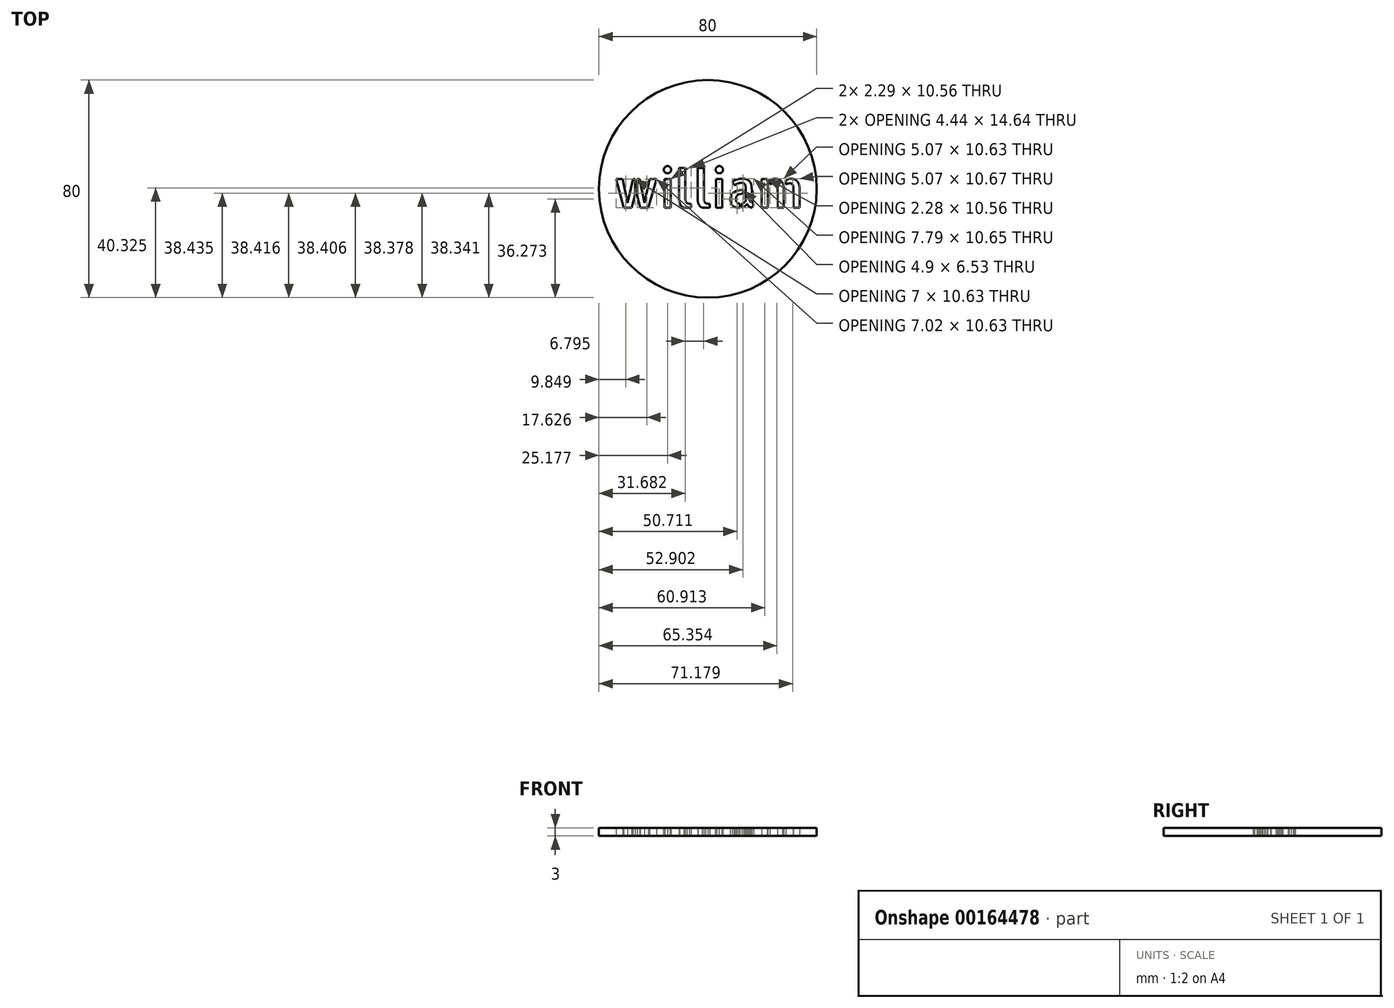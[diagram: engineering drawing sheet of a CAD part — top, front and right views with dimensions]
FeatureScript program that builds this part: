
annotation { "Feature Type Name" : "Feature", "Feature Type Description" : "" }
export const myFeature = defineFeature(function(context is Context, id is Id, definition is map)
    precondition{}
    {
        {
            var Q0;
            Q0=qCreatedBy(makeId("Top.planeOp"),FACE);
            var sketch = newSketch(context, id + "F0", { "sketchPlane" : qUnion([Q0])});
            skCircle(sketch, "E0", {"center": v(0, 0) * mm, "radius": 40 * mm});
            skText(sketch, "E1", { "text": "william", "fontName": "AllertaStencil-Regular.ttf"});
            const initialGuessF0  = {"E1": [-0.035, -0.0069, 1, 0, 0.0138]};
            skSetInitialGuess(sketch, initialGuessF0);
            skSolve(sketch);
        }
        {
            var Q0;
            Q0=makeQuery(id+"F0.imprint","IMPRINT",FACE,{"disambiguationData":[TD([[makeQuery(id+"F0.imprint","IMPRINT",EDGE,{"derivedFrom":sQuery(id+"F0.wireOp",EDGE,"E0")}),1.0]])]});
            extrude(context, id + "F1", {"entities" : qUnion([Q0]), "depth" : 3 * mm});
        }
    });
